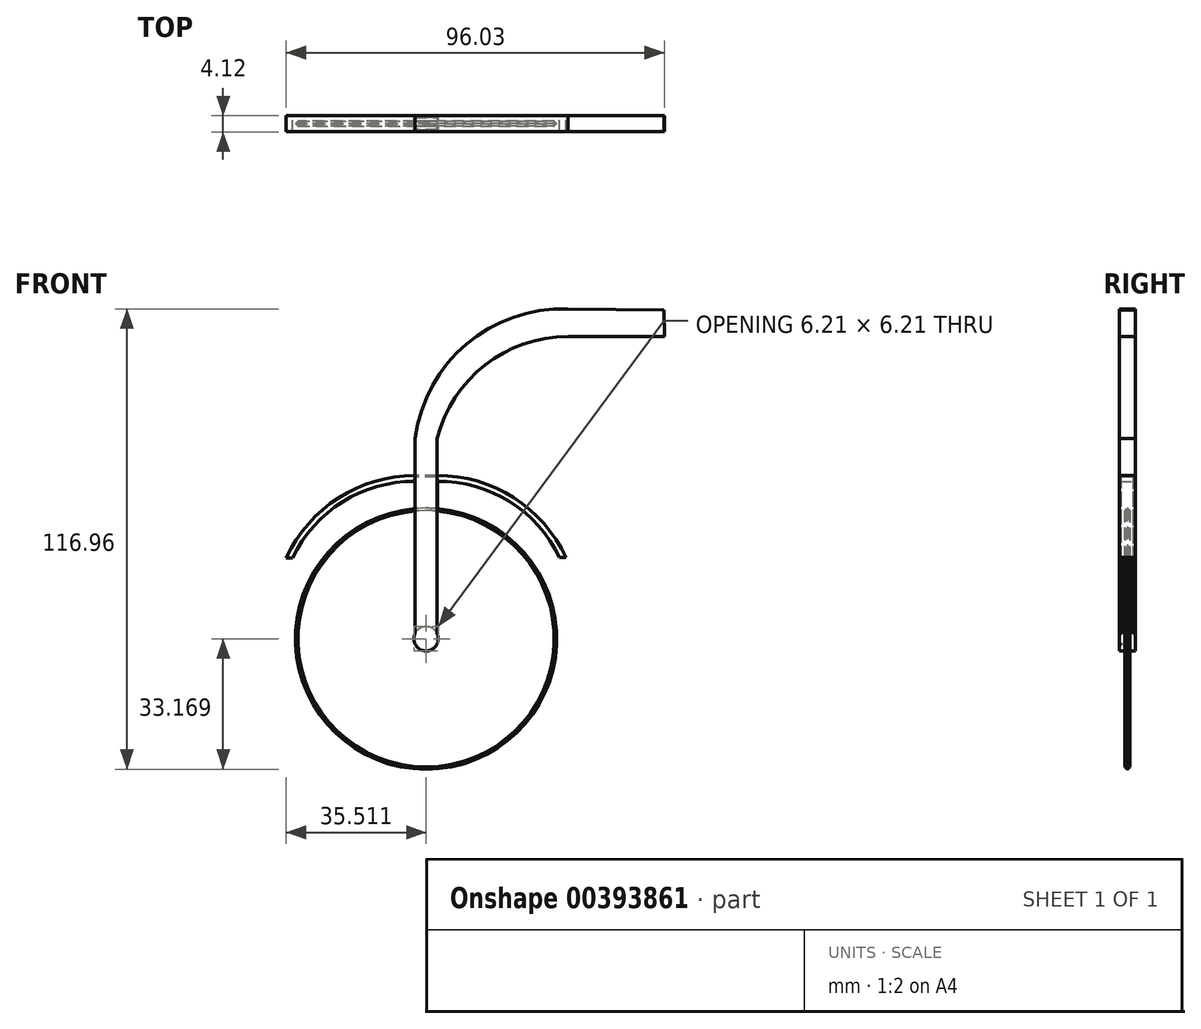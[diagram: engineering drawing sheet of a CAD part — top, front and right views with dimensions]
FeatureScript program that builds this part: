
annotation { "Feature Type Name" : "Feature", "Feature Type Description" : "" }
export const myFeature = defineFeature(function(context is Context, id is Id, definition is map)
    precondition{}
    {
        {
            var Q0;
            Q0=qCreatedBy(makeId("Front.planeOp"),FACE);
            var sketch = newSketch(context, id + "F0", { "sketchPlane" : qUnion([Q0])});
            skCircle(sketch, "E0", {"center": v(0, 0) * mm, "radius": 33.17 * mm});
            skSolve(sketch);
        }
        {
            var Q0;
            Q0=makeQuery(id+"F0.imprint","IMPRINT",FACE,{"disambiguationData":[TD([[makeQuery(id+"F0.imprint","IMPRINT",EDGE,{"derivedFrom":sQuery(id+"F0.wireOp",EDGE,"E0")}),1.0]])]});
            extrude(context, id + "F1", {"entities" : qUnion([Q0]), "depth" : 0.64 * mm, "hasSecondDirection" : true, "secondDirectionOppositeDirection" : true, "secondDirectionDepth" : 0.64 * mm});
        }
        {
            var Q0;
            Q0=makeQuery(id+"F1.opExtrude","CAP_EDGE",EDGE,{"disambiguationData":[OSD([sQuery(id+"F0.wireOp",EDGE,"E0")])],"isStart":false});
            var Q1;
            Q1=makeQuery(id+"F1.opExtrude","CAP_FACE",FACE,{"disambiguationData":[OSD([sQuery(id+"F0.wireOp",EDGE,"E0")])],"isStart":true});
            chamfer(context, id + "F2", {"entities" : qUnion([Q0, Q1]), "width" : 0.6 * mm, "tangentPropagation" : true});
        }
        {
            var Q0;
            Q0=qCreatedBy(makeId("Front.planeOp"),FACE);
            var sketch = newSketch(context, id + "F3", { "sketchPlane" : qUnion([Q0])});
            skCircle(sketch, "E1", {"center": v(0, 0) * mm, "radius": 3.1 * mm});
            skSolve(sketch);
        }
        {
            var Q0;
            Q0 = qSketchRegion(id + "F3", true);
            extrude(context, id + "F4", {"entities" : qUnion([Q0]), "operationType" : NewBodyOperationType.ADD, "depth" : 2.06 * mm, "hasSecondDirection" : true, "secondDirectionOppositeDirection" : true, "secondDirectionDepth" : 2.06 * mm});
        }
        {
            var Q0;
            Q0=makeQuery(id+"F4.opExtrude","CAP_FACE",FACE,{"disambiguationData":[OSD([sQuery(id+"F3.wireOp",EDGE,"E1")])],"isStart":false});
            var sketch = newSketch(context, id + "F5", { "sketchPlane" : qUnion([Q0])});
            skLineSegment(sketch, "E2.bottom", {"start": v(-2.76, -1.42) * mm, "end": v(2.83, -1.42) * mm});
            skLineSegment(sketch, "E2.top", {"start": v(-2.76, 41.08) * mm, "end": v(2.83, 41.08) * mm});
            skLineSegment(sketch, "E2.left", {"start": v(-2.76, -1.42) * mm, "end": v(-2.76, 41.08) * mm});
            skLineSegment(sketch, "E2.right", {"start": v(2.83, -1.42) * mm, "end": v(2.83, 41.08) * mm});
            skSolve(sketch);
        }
        {
            var Q0;
            Q0 = qSketchRegion(id + "F5", true);
            extrude(context, id + "F6", {"entities" : qUnion([Q0]), "operationType" : NewBodyOperationType.ADD, "oppositeDirection" : true, "depth" : 0.53 * mm});
        }
        {
            var Q0;
            Q0=makeQuery(id+"F4.opExtrude","CAP_FACE",FACE,{"disambiguationData":[OSD([sQuery(id+"F3.wireOp",EDGE,"E1")])],"isStart":true});
            var sketch = newSketch(context, id + "F7", { "sketchPlane" : qUnion([Q0])});
            skLineSegment(sketch, "E3.bottom", {"start": v(-2.88, -1.16) * mm, "end": v(2.86, -1.16) * mm});
            skLineSegment(sketch, "E3.top", {"start": v(-2.88, 41.47) * mm, "end": v(2.86, 41.47) * mm});
            skLineSegment(sketch, "E3.left", {"start": v(-2.88, -1.16) * mm, "end": v(-2.88, 41.47) * mm});
            skLineSegment(sketch, "E3.right", {"start": v(2.86, -1.16) * mm, "end": v(2.86, 41.47) * mm});
            skSolve(sketch);
        }
        {
            var Q0;
            Q0 = qSketchRegion(id + "F7", true);
            extrude(context, id + "F8", {"entities" : qUnion([Q0]), "operationType" : NewBodyOperationType.ADD, "oppositeDirection" : true, "depth" : 0.5 * mm});
        }
        {
            var Q0;
            Q0=makeQuery(id+"F8.boolean.opBoolean","MERGE",FACE,{"derivedFrom":[makeQuery(id+"F4.opExtrude","CAP_FACE",FACE,{"disambiguationData":[OSD([sQuery(id+"F3.wireOp",EDGE,"E1")])],"isStart":true}),makeQuery(id+"F8.opExtrude","CAP_FACE",FACE,{"disambiguationData":[OSD([sQuery(id+"F7.wireOp",EDGE,"E3.bottom"),sQuery(id+"F7.wireOp",EDGE,"E3.top"),sQuery(id+"F7.wireOp",EDGE,"E3.left"),sQuery(id+"F7.wireOp",EDGE,"E3.right")])],"isStart":true})]});
            var sketch = newSketch(context, id + "F9", { "sketchPlane" : qUnion([Q0])});
            skLineSegment(sketch, "E4", {"start": v(-2.88, 41.47) * mm, "end": v(2.86, 41.47) * mm});
            skLineSegment(sketch, "E5", {"start": v(0, 41.47) * mm, "end": v(-0.01, 30.86) * mm, "construction": true});
            skPoint(sketch, "E5.endSnap0", {"position": v(-0.01, 41.47) * mm});
            skArc(sketch, "E6", {"start": v(35.5, 20.53) * mm, "mid": v(22.25, 35.79) * mm, "end": v(2.86, 41.47) * mm});
            skArc(sketch, "E7.MirrorCS", {"start": v(-35.55, 20.6) * mm, "mid": v(-22.26, 35.83) * mm, "end": v(-2.86, 41.48) * mm});
            skLineSegment(sketch, "E8", {"start": v(-35.55, 20.6) * mm, "end": v(-33.92, 20.6) * mm});
            skArc(sketch, "E9", {"start": v(-2.88, 39.98) * mm, "mid": v(-21.23, 34.83) * mm, "end": v(-33.92, 20.6) * mm});
            skLineSegment(sketch, "E10", {"start": v(-2.88, 39.98) * mm, "end": v(-2.86, 41.48) * mm});
            skArc(sketch, "E11.MirrorCS", {"start": v(2.88, 39.98) * mm, "mid": v(21.21, 34.78) * mm, "end": v(33.88, 20.54) * mm});
            skLineSegment(sketch, "E12.MirrorCS", {"start": v(35.5, 20.53) * mm, "end": v(33.88, 20.54) * mm});
            skLineSegment(sketch, "E13.MirrorCS", {"start": v(2.88, 39.98) * mm, "end": v(2.86, 41.47) * mm});
            skSolve(sketch);
        }
        {
            var Q0;
            Q0 = qSketchRegion(id + "F9", true);
            extrude(context, id + "F10", {"entities" : qUnion([Q0]), "operationType" : NewBodyOperationType.ADD, "oppositeDirection" : true, "depth" : 4.1 * mm});
        }
        {
            var Q0;
            Q0=makeQuery(id+"F6.boolean.opBoolean","MERGE",FACE,{"derivedFrom":[makeQuery(id+"F4.opExtrude","CAP_FACE",FACE,{"disambiguationData":[OSD([sQuery(id+"F3.wireOp",EDGE,"E1")])],"isStart":false}),makeQuery(id+"F6.opExtrude","CAP_FACE",FACE,{"disambiguationData":[OSD([sQuery(id+"F5.wireOp",EDGE,"E2.bottom"),sQuery(id+"F5.wireOp",EDGE,"E2.top"),sQuery(id+"F5.wireOp",EDGE,"E2.left"),sQuery(id+"F5.wireOp",EDGE,"E2.right")])],"isStart":true})]});
            var sketch = newSketch(context, id + "F11", { "sketchPlane" : qUnion([Q0])});
            skLineSegment(sketch, "E14.bottom", {"start": v(-2.76, 41.08) * mm, "end": v(2.78, 41.08) * mm});
            skLineSegment(sketch, "E14.top", {"start": v(-2.76, 50.9) * mm, "end": v(2.78, 50.9) * mm});
            skLineSegment(sketch, "E14.left", {"start": v(-2.76, 41.08) * mm, "end": v(-2.76, 50.9) * mm});
            skLineSegment(sketch, "E14.right", {"start": v(2.78, 41.08) * mm, "end": v(2.78, 50.9) * mm});
            skArc(sketch, "E15", {"start": v(36.04, 76.77) * mm, "mid": v(14.98, 69.52) * mm, "end": v(2.78, 50.9) * mm});
            skArc(sketch, "E16", {"start": v(36.04, 83.77) * mm, "mid": v(10.25, 74.87) * mm, "end": v(-2.76, 50.9) * mm});
            skLineSegment(sketch, "E17", {"start": v(36.04, 76.77) * mm, "end": v(60.52, 76.81) * mm});
            skLineSegment(sketch, "E18", {"start": v(60.52, 76.81) * mm, "end": v(60.5, 83.52) * mm});
            skLineSegment(sketch, "E19", {"start": v(60.5, 83.52) * mm, "end": v(36.04, 83.77) * mm});
            skSolve(sketch);
        }
        {
            var Q0;
            Q0 = qSketchRegion(id + "F11", true);
            extrude(context, id + "F12", {"entities" : qUnion([Q0]), "operationType" : NewBodyOperationType.ADD, "oppositeDirection" : true, "depth" : 4.06 * mm});
        }
    });
